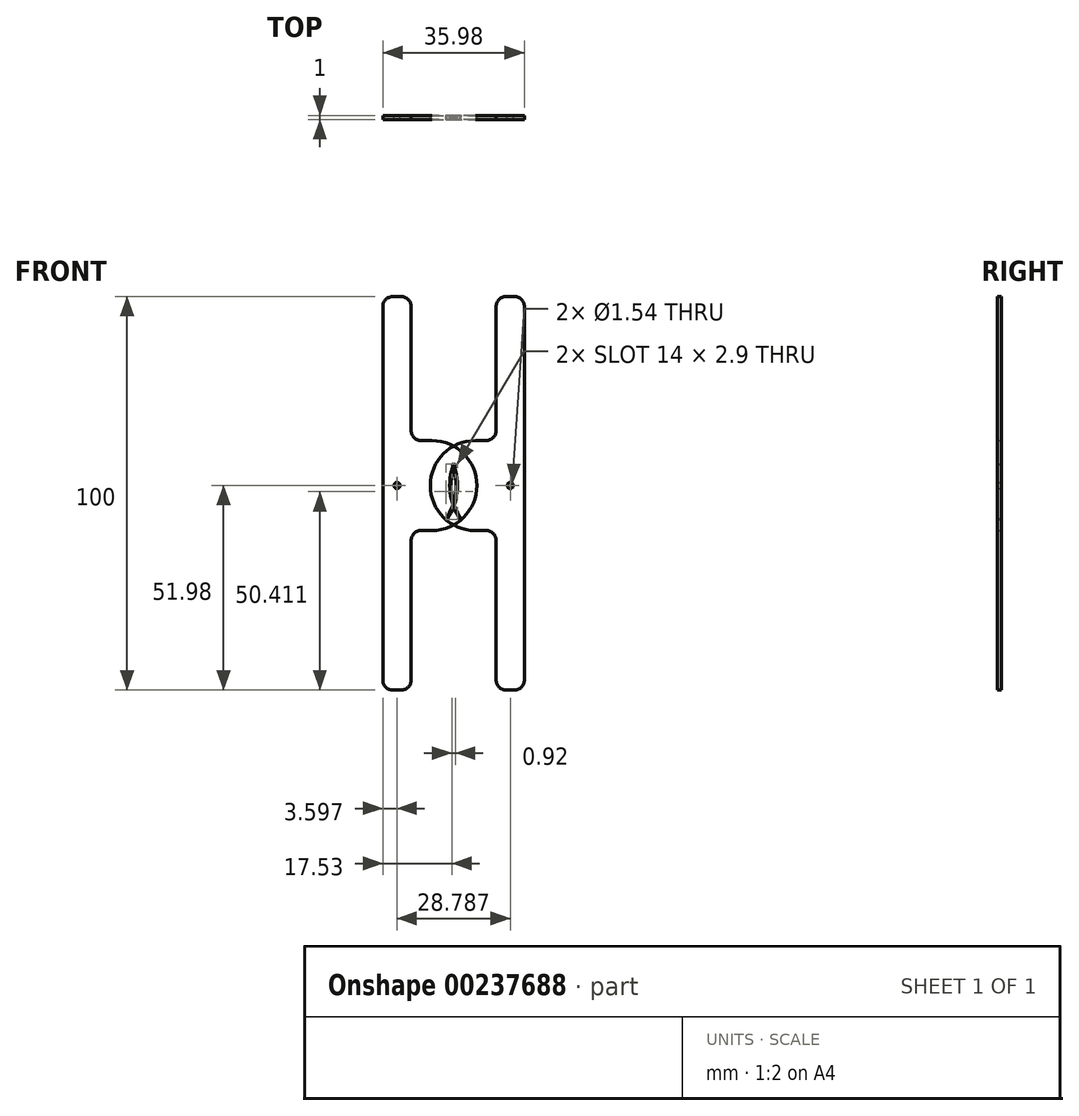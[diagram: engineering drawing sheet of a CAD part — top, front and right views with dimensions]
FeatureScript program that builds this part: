
annotation { "Feature Type Name" : "Feature", "Feature Type Description" : "" }
export const myFeature = defineFeature(function(context is Context, id is Id, definition is map)
    precondition{}
    {
        {
            var Q0;
            Q0=qCreatedBy(makeId("Front.planeOp"),FACE);
            var sketch = newSketch(context, id + "F0", { "sketchPlane" : qUnion([Q0])});
            skLineSegment(sketch, "E0", {"start": v(-18, 59.45) * mm, "end": v(-18, -40.55) * mm});
            skLineSegment(sketch, "E1", {"start": v(-18, -40.55) * mm, "end": v(-10.8, -40.55) * mm});
            skLineSegment(sketch, "E2", {"start": v(-10.8, -40.55) * mm, "end": v(-10.8, 0) * mm});
            skLineSegment(sketch, "E3", {"start": v(-10.8, 0) * mm, "end": v(5.93, 0) * mm});
            skLineSegment(sketch, "E4", {"start": v(5.93, 0) * mm, "end": v(5.93, 22.86) * mm});
            skLineSegment(sketch, "E5", {"start": v(5.93, 22.86) * mm, "end": v(-10.8, 22.86) * mm});
            skLineSegment(sketch, "E6", {"start": v(-10.8, 22.86) * mm, "end": v(-10.8, 59.45) * mm});
            skLineSegment(sketch, "E7", {"start": v(-10.8, 59.45) * mm, "end": v(-18, 59.45) * mm});
            skPoint(sketch, "E8.startSnap0", {"position": v(-14.4, -40.55) * mm});
            skPoint(sketch, "E8.startSnap1", {"position": v(5.93, 11.43) * mm});
            skCircle(sketch, "E9", {"center": v(-14.4, 11.43) * mm, "radius": 0.77 * mm});
            skArc(sketch, "E10", {"start": v(0, 16.86) * mm, "mid": v(0.89, 9.67) * mm, "end": v(-1.62, 2.86) * mm});
            skArc(sketch, "E11.0", {"start": v(-0.33, 16.74) * mm, "mid": v(0.54, 9.7) * mm, "end": v(-1.91, 3.06) * mm});
            skLineSegment(sketch, "E12", {"start": v(-0.33, 16.74) * mm, "end": v(0, 16.86) * mm});
            skLineSegment(sketch, "E13", {"start": v(-1.91, 3.06) * mm, "end": v(-1.62, 2.86) * mm});
            skSolve(sketch);
        }
        {
            var Q0;
            Q0=makeQuery(id+"F0.imprint","IMPRINT",FACE,{"disambiguationData":[TD([[makeQuery(id+"F0.imprint","IMPRINT",EDGE,{"derivedFrom":sQuery(id+"F0.wireOp",EDGE,"E0")}),1.0]])]});
            extrude(context, id + "F1", {"entities" : qUnion([Q0]), "depth" : 1 * mm});
        }
        {
            var Q0;
            Q0=makeQuery(id+"F1.opExtrude","SWEPT_EDGE",EDGE,{"disambiguationData":[OSD([sQuery(id+"F0.wireOp",EDGE,"E3"),sQuery(id+"F0.wireOp",EDGE,"E4")])]});
            var Q1;
            Q1=makeQuery(id+"F1.opExtrude","SWEPT_EDGE",EDGE,{"disambiguationData":[OSD([sQuery(id+"F0.wireOp",EDGE,"E4"),sQuery(id+"F0.wireOp",EDGE,"E5")])]});
            fillet(context, id + "F2", {"entities" : qUnion([Q0, Q1]), "radius" : 11.43 * mm, "tangentPropagation" : true, "allowEdgeOverflow" : false});
        }
        {
            var Q0;
            Q0=makeQuery(id+"F1.opExtrude","SWEPT_EDGE",EDGE,{"disambiguationData":[OSD([sQuery(id+"F0.wireOp",EDGE,"E1"),sQuery(id+"F0.wireOp",EDGE,"E2")])]});
            var Q1;
            Q1=makeQuery(id+"F1.opExtrude","SWEPT_EDGE",EDGE,{"disambiguationData":[OSD([sQuery(id+"F0.wireOp",EDGE,"E0"),sQuery(id+"F0.wireOp",EDGE,"E1")])]});
            var Q2;
            Q2=makeQuery(id+"F1.opExtrude","SWEPT_EDGE",EDGE,{"disambiguationData":[OSD([sQuery(id+"F0.wireOp",EDGE,"E2"),sQuery(id+"F0.wireOp",EDGE,"E3")])]});
            var Q3;
            Q3=makeQuery(id+"F1.opExtrude","SWEPT_EDGE",EDGE,{"disambiguationData":[OSD([sQuery(id+"F0.wireOp",EDGE,"E5"),sQuery(id+"F0.wireOp",EDGE,"E6")])]});
            var Q4;
            Q4=makeQuery(id+"F1.opExtrude","SWEPT_EDGE",EDGE,{"disambiguationData":[OSD([sQuery(id+"F0.wireOp",EDGE,"E6"),sQuery(id+"F0.wireOp",EDGE,"E7")])]});
            var Q5;
            Q5=makeQuery(id+"F1.opExtrude","SWEPT_EDGE",EDGE,{"disambiguationData":[OSD([sQuery(id+"F0.wireOp",EDGE,"E0"),sQuery(id+"F0.wireOp",EDGE,"E7")])]});
            fillet(context, id + "F3", {"entities" : qUnion([Q0, Q1, Q2, Q3, Q4, Q5]), "radius" : 2.54 * mm, "tangentPropagation" : true, "allowEdgeOverflow" : false});
        }
        {
            var Q0;
            Q0=makeQuery(id+"F1.opExtrude","SWEPT_BODY",BODY,{"disambiguationData":[OSD([sQuery(id+"F0.wireOp",EDGE,"E0"),sQuery(id+"F0.wireOp",EDGE,"E1"),sQuery(id+"F0.wireOp",EDGE,"E2"),sQuery(id+"F0.wireOp",EDGE,"E3"),sQuery(id+"F0.wireOp",EDGE,"E4"),sQuery(id+"F0.wireOp",EDGE,"E5"),sQuery(id+"F0.wireOp",EDGE,"E6"),sQuery(id+"F0.wireOp",EDGE,"E7"),sQuery(id+"F0.wireOp",EDGE,"E9"),sQuery(id+"F0.wireOp",EDGE,"E10"),sQuery(id+"F0.wireOp",EDGE,"E11.0"),sQuery(id+"F0.wireOp",EDGE,"E12"),sQuery(id+"F0.wireOp",EDGE,"E13")])]});
            var Q1;
            Q1=qCreatedBy(makeId("Right.planeOp"),FACE);
            mirror(context, id + "F4", {"entities" : qUnion([Q0]), "mirrorPlane" : qUnion([Q1])});
        }
    });
